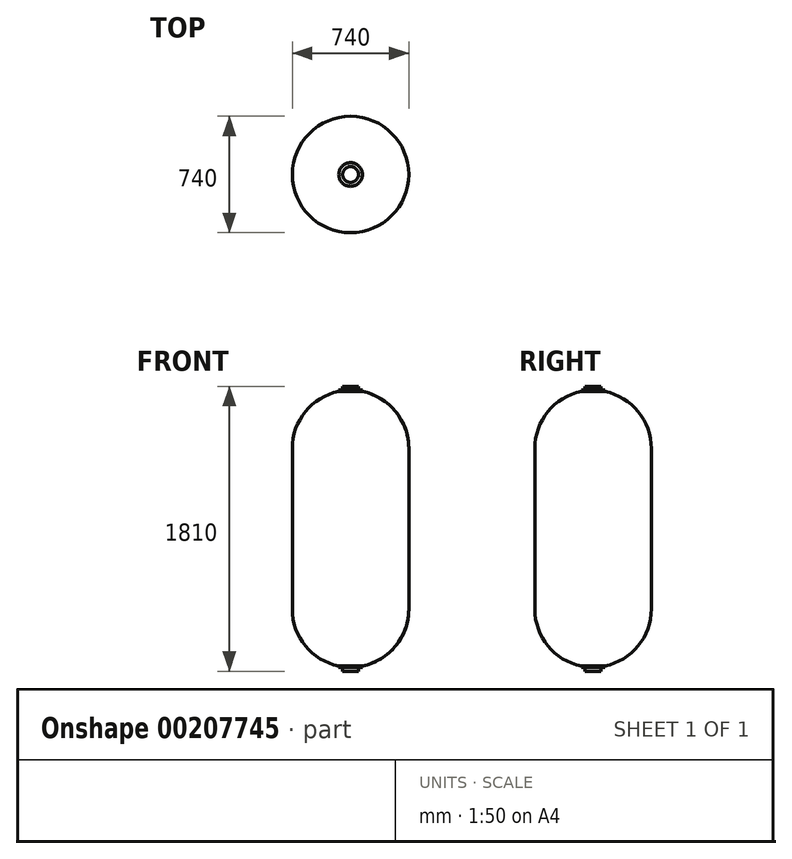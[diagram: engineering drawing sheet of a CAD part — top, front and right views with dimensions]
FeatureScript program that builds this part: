
annotation { "Feature Type Name" : "Feature", "Feature Type Description" : "" }
export const myFeature = defineFeature(function(context is Context, id is Id, definition is map)
    precondition{}
    {
        {
            var Q0;
            Q0=qCreatedBy(makeId("Front.planeOp"),FACE);
            var sketch = newSketch(context, id + "F0", { "sketchPlane" : qUnion([Q0])});
            skArc(sketch, "E0", {"start": v(75, 7.68) * mm, "mid": v(286.92, 136.39) * mm, "end": v(370, 370) * mm});
            skLineSegment(sketch, "E1", {"start": v(370, 370) * mm, "end": v(370, 1390) * mm});
            skArc(sketch, "E2", {"start": v(370, 1390) * mm, "mid": v(286.92, 1623.61) * mm, "end": v(75, 1752.32) * mm});
            skLineSegment(sketch, "E3", {"start": v(0, 1760) * mm, "end": v(0, 0) * mm});
            skLineSegment(sketch, "E4", {"start": v(75, 7.68) * mm, "end": v(75, 0) * mm});
            skLineSegment(sketch, "E5", {"start": v(75, 0) * mm, "end": v(50, 0) * mm});
            skLineSegment(sketch, "E6", {"start": v(50, 0) * mm, "end": v(50, -25) * mm});
            skLineSegment(sketch, "E7", {"start": v(50, -25) * mm, "end": v(0, -25) * mm});
            skLineSegment(sketch, "E8", {"start": v(0, -25) * mm, "end": v(0, 0) * mm});
            skLineSegment(sketch, "E9", {"start": v(75, 1752.32) * mm, "end": v(75, 1760) * mm});
            skLineSegment(sketch, "E10", {"start": v(75, 1760) * mm, "end": v(50, 1760) * mm});
            skLineSegment(sketch, "E11", {"start": v(50, 1760) * mm, "end": v(50, 1785) * mm});
            skLineSegment(sketch, "E12", {"start": v(50, 1785) * mm, "end": v(0, 1785) * mm});
            skLineSegment(sketch, "E13", {"start": v(0, 1785) * mm, "end": v(0, 1760) * mm});
            skSolve(sketch);
        }
        {
            var Q0;
            Q0=makeQuery(id+"F0.imprint","IMPRINT",FACE,{"disambiguationData":[TD([[makeQuery(id+"F0.imprint","IMPRINT",EDGE,{"derivedFrom":sQuery(id+"F0.wireOp",EDGE,"E0")}),1.0]])]});
            var Q1;
            Q1=sQuery(id+"F0.wireOp",EDGE,"E3");
            revolve(context, id + "F1", {"entities" : qUnion([Q0]), "axis" : qUnion([Q1]), "revolveType" : RevolveType.FULL});
        }
    });
